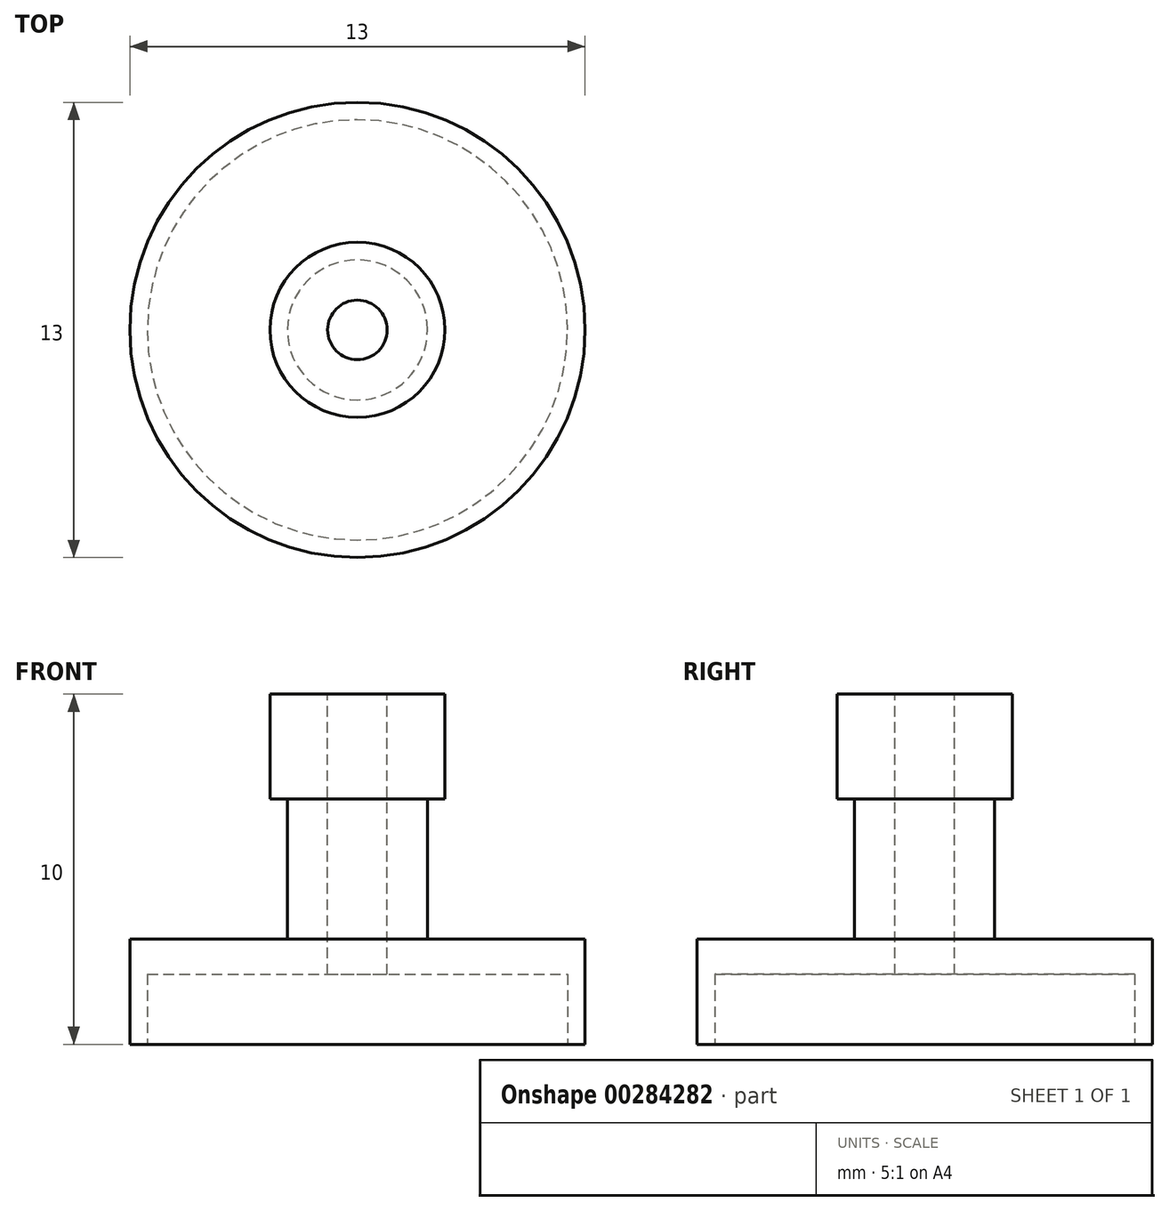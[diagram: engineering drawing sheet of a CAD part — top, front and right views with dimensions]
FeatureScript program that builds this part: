
annotation { "Feature Type Name" : "Feature", "Feature Type Description" : "" }
export const myFeature = defineFeature(function(context is Context, id is Id, definition is map)
    precondition{}
    {
        {
            var Q0;
            Q0=qCreatedBy(makeId("Top.planeOp"),FACE);
            var sketch = newSketch(context, id + "F0", { "sketchPlane" : qUnion([Q0])});
            skCircle(sketch, "E0", {"center": v(0, 0) * mm, "radius": 6.5 * mm});
            skSolve(sketch);
        }
        {
            var Q0;
            Q0=makeQuery(id+"F0.imprint","IMPRINT",FACE,{"disambiguationData":[TD([[makeQuery(id+"F0.imprint","IMPRINT",EDGE,{"derivedFrom":sQuery(id+"F0.wireOp",EDGE,"E0")}),1.0]])]});
            extrude(context, id + "F1", {"entities" : qUnion([Q0]), "depth" : 3 * mm});
        }
        {
            var Q0;
            Q0=makeQuery(id+"F1.opExtrude","CAP_FACE",FACE,{"disambiguationData":[OSD([sQuery(id+"F0.wireOp",EDGE,"E0")])],"isStart":false});
            var sketch = newSketch(context, id + "F2", { "sketchPlane" : qUnion([Q0])});
            skCircle(sketch, "E1", {"center": v(0, 0) * mm, "radius": 2 * mm});
            skSolve(sketch);
        }
        {
            var Q0;
            Q0=makeQuery(id+"F2.imprint","IMPRINT",FACE,{"disambiguationData":[TD([[makeQuery(id+"F2.imprint","IMPRINT",EDGE,{"derivedFrom":sQuery(id+"F2.wireOp",EDGE,"E1")}),1.0]])]});
            var Q1;
            Q1=sQuery(id+"F2.wireOp",EDGE,"E1");
            extrude(context, id + "F3", {"entities" : qUnion([Q0]), "operationType" : NewBodyOperationType.ADD, "surfaceEntities" : qUnion([Q1]), "depth" : 4 * mm});
        }
        {
            var Q0;
            Q0=makeQuery(id+"F3.opExtrude","CAP_FACE",FACE,{"disambiguationData":[OSD([sQuery(id+"F2.wireOp",EDGE,"E1")])],"isStart":false});
            var sketch = newSketch(context, id + "F4", { "sketchPlane" : qUnion([Q0])});
            skCircle(sketch, "E2", {"center": v(0, 0) * mm, "radius": 2.5 * mm});
            skSolve(sketch);
        }
        {
            var Q0;
            Q0 = qSketchRegion(id + "F4", true);
            var Q1;
            Q1=sQuery(id+"F4.wireOp",EDGE,"E2");
            extrude(context, id + "F5", {"entities" : qUnion([Q0]), "operationType" : NewBodyOperationType.ADD, "surfaceEntities" : qUnion([Q1]), "depth" : 3 * mm});
        }
        {
            var Q0;
            Q0=makeQuery(id+"F1.opExtrude","CAP_FACE",FACE,{"disambiguationData":[OSD([sQuery(id+"F0.wireOp",EDGE,"E0")])],"isStart":true});
            var sketch = newSketch(context, id + "F6", { "sketchPlane" : qUnion([Q0])});
            skCircle(sketch, "E3", {"center": v(0, 0) * mm, "radius": 6 * mm});
            skSolve(sketch);
        }
        {
            var Q0;
            Q0=makeQuery(id+"F6.imprint","IMPRINT",FACE,{"disambiguationData":[TD([[makeQuery(id+"F6.imprint","IMPRINT",EDGE,{"derivedFrom":sQuery(id+"F6.wireOp",EDGE,"E3")}),1.0]])]});
            extrude(context, id + "F7", {"entities" : qUnion([Q0]), "operationType" : NewBodyOperationType.REMOVE, "oppositeDirection" : true, "depth" : 2 * mm});
        }
        {
            var Q0;
            Q0=makeQuery(id+"F5.opExtrude","CAP_FACE",FACE,{"disambiguationData":[OSD([sQuery(id+"F4.wireOp",EDGE,"E2")])],"isStart":false});
            var sketch = newSketch(context, id + "F8", { "sketchPlane" : qUnion([Q0])});
            skCircle(sketch, "E4", {"center": v(0, 0) * mm, "radius": 0.85 * mm});
            skSolve(sketch);
        }
        {
            var Q0;
            Q0=makeQuery(id+"F8.imprint","IMPRINT",FACE,{"disambiguationData":[TD([[makeQuery(id+"F8.imprint","IMPRINT",EDGE,{"derivedFrom":sQuery(id+"F8.wireOp",EDGE,"E4")}),1.0]])]});
            var Q1;
            Q1=sQuery(id+"F8.wireOp",EDGE,"E4");
            extrude(context, id + "F9", {"entities" : qUnion([Q0]), "operationType" : NewBodyOperationType.REMOVE, "surfaceEntities" : qUnion([Q1]), "endBound" : BoundingType.THROUGH_ALL, "oppositeDirection" : true, "depth" : 25 * mm});
        }
    });
